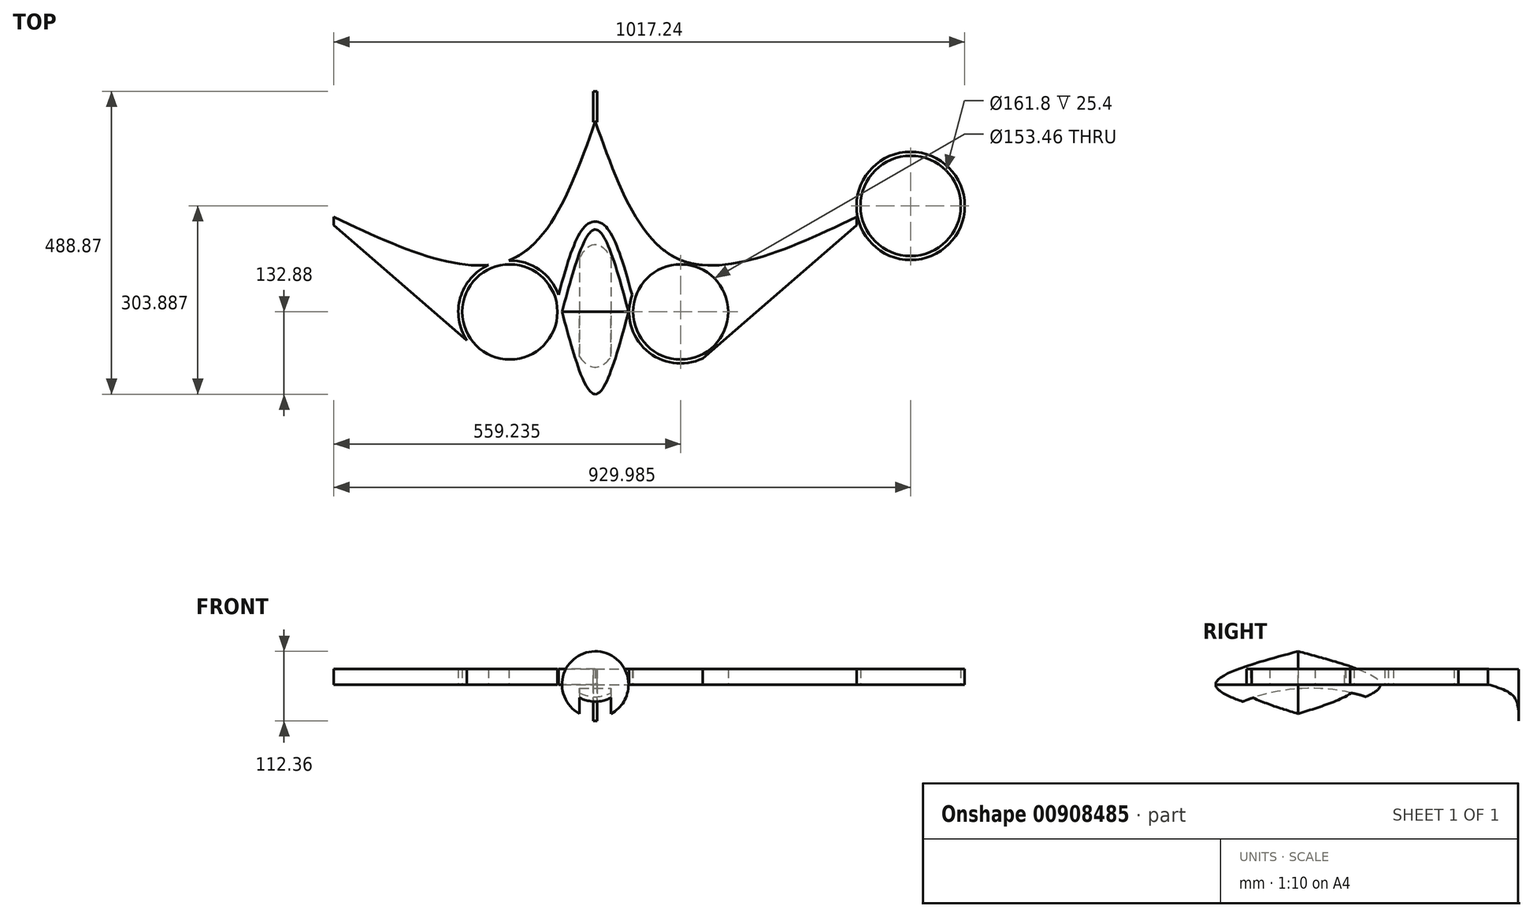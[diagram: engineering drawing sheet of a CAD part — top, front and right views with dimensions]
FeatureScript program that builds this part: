
annotation { "Feature Type Name" : "Feature", "Feature Type Description" : "" }
export const myFeature = defineFeature(function(context is Context, id is Id, definition is map)
    precondition{}
    {
        {
            var Q0;
            Q0=qCreatedBy(makeId("Top.planeOp"),FACE);
            var sketch = newSketch(context, id + "F0", { "sketchPlane" : qUnion([Q0])});
            skFitSpline(sketch, "E0", {"points": [v(-53.6, 0) * mm, v(0, -132.88) * mm, v(53.6, 0) * mm], "startDerivative": vector(107.2, -398.65) * mm, "endDerivative": vector(107.2, 398.65) * mm});
            skLineSegment(sketch, "E1", {"start": v(-53.6, 0) * mm, "end": v(53.6, 0) * mm});
            skFitSpline(sketch, "E2.MirrorCS", {"points": [v(-53.6, 0) * mm, v(0, 132.88) * mm, v(53.6, 0) * mm], "startDerivative": vector(107.2, 398.65) * mm, "endDerivative": vector(107.2, -398.65) * mm});
            skLineSegment(sketch, "E3", {"start": v(-46.29, -27.03) * mm, "end": v(-53.6, 0) * mm});
            skLineSegment(sketch, "E4", {"start": v(-46.29, 27.03) * mm, "end": v(-53.6, 0) * mm});
            skLineSegment(sketch, "E5", {"start": v(0, 132.88) * mm, "end": v(0, -132.88) * mm});
            skSolve(sketch);
        }
        {
            var Q0;
            Q0 = qSketchRegion(id + "F0", true);
            var sketch = newSketch(context, id + "F1", { "sketchPlane" : qUnion([Q0])});
            skCircle(sketch, "E6", {"center": v(137.74, 0) * mm, "radius": 76.73 * mm});
            skLineSegment(sketch, "E7", {"start": v(0, 0) * mm, "end": v(0, 75.52) * mm});
            skLineSegment(sketch, "E8", {"start": v(0, 75.52) * mm, "end": v(0, -130.45) * mm});
            skCircle(sketch, "E9.MirrorC", {"center": v(-137.74, 0) * mm, "radius": 76.73 * mm});
            skCircle(sketch, "E10.0", {"center": v(137.74, 0) * mm, "radius": 83.08 * mm});
            skCircle(sketch, "E11.MirrorC", {"center": v(-137.74, 0) * mm, "radius": 83.08 * mm});
            skFitSpline(sketch, "E12.0", {"points": [v(-65.86, 3.3) * mm, v(-63.63, 11.6) * mm, v(-59.16, 28.24) * mm, v(-52.41, 52.53) * mm, v(-46.76, 71.58) * mm, v(-42.2, 85.75) * mm, v(-38.76, 95.76) * mm, v(-35.28, 105.07) * mm, v(-31.74, 113.62) * mm, v(-28.1, 121.35) * mm, v(-24.91, 127.1) * mm, v(-22.2, 131.29) * mm, v(-20.04, 134.23) * mm, v(-17.7, 136.97) * mm, v(-15.1, 139.51) * mm, v(-12.14, 141.82) * mm, v(-9.24, 143.46) * mm, v(-6.63, 144.5) * mm, v(-4.53, 145.1) * mm, v(-2.68, 145.43) * mm, v(-1.15, 145.56) * mm, v(0, 145.6) * mm, v(1.16, 145.56) * mm, v(2.68, 145.43) * mm, v(4.53, 145.1) * mm, v(6.63, 144.5) * mm, v(9.24, 143.46) * mm, v(12.14, 141.82) * mm, v(15.1, 139.51) * mm, v(17.7, 136.97) * mm, v(20.04, 134.23) * mm, v(22.2, 131.29) * mm, v(24.91, 127.1) * mm, v(28.1, 121.35) * mm, v(31.74, 113.62) * mm, v(35.28, 105.07) * mm, v(38.76, 95.76) * mm, v(42.2, 85.75) * mm, v(46.76, 71.58) * mm, v(52.41, 52.53) * mm, v(59.16, 28.24) * mm, v(63.63, 11.6) * mm, v(65.86, 3.3) * mm]});
            skLineSegment(sketch, "E13", {"start": v(0, 75.52) * mm, "end": v(0, 307.36) * mm});
            skFitSpline(sketch, "E14", {"points": [v(0, 307.36) * mm, v(139.15, 83.07) * mm, v(457.3, 171) * mm], "startDerivative": vector(222.05, -626.73) * mm, "endDerivative": vector(683.94, 336.1) * mm});
            skFitSpline(sketch, "E15.MirrorCS", {"points": [v(0, 307.36) * mm, v(-139.15, 83.07) * mm, v(-457.3, 171) * mm], "startDerivative": vector(-222.05, -626.73) * mm, "endDerivative": vector(-683.94, 336.1) * mm});
            skLineSegment(sketch, "E16", {"start": v(173.26, -75.1) * mm, "end": v(421.49, 139.98) * mm});
            skLineSegment(sketch, "E17.MirrorCS", {"start": v(-173.26, -75.1) * mm, "end": v(-421.49, 139.98) * mm});
            skLineSegment(sketch, "E18", {"start": v(421.49, 139.98) * mm, "end": v(421.49, 153.48) * mm});
            skLineSegment(sketch, "E19.MirrorCS", {"start": v(-421.49, 139.98) * mm, "end": v(-421.49, 153.48) * mm});
            skCircle(sketch, "E20", {"center": v(508.5, 171) * mm, "radius": 87.25 * mm});
            skCircle(sketch, "E21.MirrorC", {"center": v(-508.5, 171) * mm, "radius": 87.25 * mm});
            skCircle(sketch, "E22.0", {"center": v(508.5, 171) * mm, "radius": 80.9 * mm});
            skCircle(sketch, "E23.MirrorC", {"center": v(-508.5, 171) * mm, "radius": 80.9 * mm});
            skLineSegment(sketch, "E24.extension", {"start": v(-58.53, 30.38) * mm, "end": v(-59.34, 27.46) * mm});
            skSolve(sketch);
        }
        {
            var Q0;
            {var subQ5=sQuery(id+"F1.wireOp",EDGE,"E18");Q0=makeQuery(id+"F1.imprint","IMPRINT",FACE,{"disambiguationData":[TD([[makeQuery(id+"F1.imprint","IMPRINT",EDGE,{"derivedFrom":subQ5}),1.0]])]});}
            var Q1;
            {var subQ0=sQuery(id+"F1.wireOp",EDGE,"E12.0");var subQ1=sQuery(id+"F1.wireOp",EDGE,"E10.0");var subQ2=makeQuery(id+"F1.imprint","INTERSECT",VERTEX,{"derivedFrom":[subQ1,subQ0]});Q1=makeQuery(id+"F1.imprint","IMPRINT",FACE,{"disambiguationData":[TD([[makeQuery(id+"F1.imprint","IMPRINT",EDGE,{"disambiguationData":[TD([[subQ2,1.0]])],"derivedFrom":subQ1}),-1.0]])]});}
            var Q2;
            {var subQ0=sQuery(id+"F1.wireOp",EDGE,"E24.extension");var subQ7=sQuery(id+"F1.wireOp",EDGE,"E12.0");var subQ9=makeQuery(id+"F1.imprint","INTERSECT",VERTEX,{"derivedFrom":[subQ7,subQ0]});Q2=makeQuery(id+"F1.imprint","IMPRINT",FACE,{"disambiguationData":[TD([[makeQuery(id+"F1.imprint","IMPRINT",EDGE,{"disambiguationData":[TD([[subQ9,-1.0]])],"derivedFrom":subQ7}),1.0]])]});}
            var Q3;
            {var subQ0=sQuery(id+"F1.wireOp",EDGE,"E19.MirrorCS");Q3=makeQuery(id+"F1.imprint","IMPRINT",FACE,{"disambiguationData":[TD([[makeQuery(id+"F1.imprint","IMPRINT",EDGE,{"derivedFrom":subQ0}),-1.0]])]});}
            var Q4;
            Q4=makeQuery(id+"F1.imprint","IMPRINT",FACE,{"disambiguationData":[TD([[makeQuery(id+"F1.imprint","IMPRINT",EDGE,{"derivedFrom":sQuery(id+"F1.wireOp",EDGE,"E9.MirrorC")}),1.0]])]});
            var Q5;
            Q5=makeQuery(id+"F1.imprint","IMPRINT",FACE,{"disambiguationData":[TD([[makeQuery(id+"F1.imprint","IMPRINT",EDGE,{"derivedFrom":sQuery(id+"F1.wireOp",EDGE,"E6")}),-1.0]])]});
            var Q6;
            Q6=makeQuery(id+"F1.imprint","IMPRINT",FACE,{"disambiguationData":[TD([[makeQuery(id+"F1.imprint","IMPRINT",EDGE,{"derivedFrom":sQuery(id+"F1.wireOp",EDGE,"E20")}),1.0]])]});
            var Q7;
            Q7=makeQuery(id+"F1.imprint","IMPRINT",FACE,{"disambiguationData":[TD([[makeQuery(id+"F1.imprint","IMPRINT",EDGE,{"derivedFrom":sQuery(id+"F1.wireOp",EDGE,"E21.MirrorC")}),-1.0]])]});
            extrude(context, id + "F2", {"entities" : qUnion([Q0, Q1, Q2, Q3, Q4, Q5, Q6, Q7]), "depth" : 25.4 * mm, "offsetDistance" : 25.4 * mm});
        }
        {
            var Q0;
            {var subQ0=sQuery(id+"F0.wireOp",EDGE,"E2.MirrorCS");var subQ3=sQuery(id+"F0.wireOp",EDGE,"E5");var subQ5=makeQuery(id+"F0.imprint","INTERSECT",VERTEX,{"derivedFrom":[subQ0,subQ3]});Q0=makeQuery(id+"F0.imprint","IMPRINT",FACE,{"disambiguationData":[TD([[makeQuery(id+"F0.imprint","IMPRINT",EDGE,{"disambiguationData":[TD([[subQ5,-1.0]])],"derivedFrom":subQ3}),1.0]])]});}
            var Q1;
            {var subQ1=sQuery(id+"F0.wireOp",EDGE,"E0");var subQ3=sQuery(id+"F0.wireOp",EDGE,"E5");var subQ4=makeQuery(id+"F0.imprint","INTERSECT",VERTEX,{"derivedFrom":[subQ1,subQ3]});Q1=makeQuery(id+"F0.imprint","IMPRINT",FACE,{"disambiguationData":[TD([[makeQuery(id+"F0.imprint","IMPRINT",EDGE,{"disambiguationData":[TD([[subQ4,1.0]])],"derivedFrom":subQ3}),1.0]])]});}
            var Q2;
            Q2=sQuery(id+"F0.wireOp",EDGE,"E5");
            revolve(context, id + "F3", {"surfaceOperationType" : NewSurfaceOperationType.NEW, "entities" : qUnion([Q0, Q1]), "axis" : qUnion([Q2]), "revolveType" : RevolveType.FULL});
        }
        {
            var Q0;
            Q0=qCreatedBy(makeId("Right.planeOp"),FACE);
            var sketch = newSketch(context, id + "F4", { "sketchPlane" : qUnion([Q0])});
            skArc(sketch, "E25", {"start": v(116.82, -22.27) * mm, "mid": v(12.81, -6.12) * mm, "end": v(-90.17, -27.87) * mm});
            skLineSegment(sketch, "E26", {"start": v(116.82, -22.27) * mm, "end": v(0, -56.15) * mm});
            skLineSegment(sketch, "E27", {"start": v(0, -56.15) * mm, "end": v(-90.17, -27.87) * mm});
            skSolve(sketch);
        }
        {
            var Q0;
            Q0 = qSketchRegion(id + "F4", true);
            extrude(context, id + "F5", {"entities" : qUnion([Q0]), "operationType" : NewBodyOperationType.REMOVE, "oppositeDirection" : true, "depth" : 25.4 * mm, "offsetDistance" : 25.4 * mm, "hasSecondDirection" : true, "secondDirectionOppositeDirection" : false, "secondDirectionDepth" : 25.4 * mm});
        }
        {
            var Q0;
            Q0=qCreatedBy(makeId("Right.planeOp"),FACE);
            var sketch = newSketch(context, id + "F6", { "sketchPlane" : qUnion([Q0])});
            skFitSpline(sketch, "E28", {"points": [v(306.28, 0) * mm, v(348.43, -20.22) * mm, v(355.99, -58.76) * mm], "startDerivative": vector(97.73, -27.83) * mm, "endDerivative": vector(0.26, -90.6) * mm});
            skLineSegment(sketch, "E29", {"start": v(355.99, -58.76) * mm, "end": v(355.94, 0) * mm});
            skLineSegment(sketch, "E30", {"start": v(355.94, 0) * mm, "end": v(306.28, 0) * mm});
            skLineSegment(sketch, "E31", {"start": v(355.94, 0) * mm, "end": v(355.94, 24.64) * mm});
            skLineSegment(sketch, "E32", {"start": v(355.94, 24.64) * mm, "end": v(306.28, 25) * mm});
            skLineSegment(sketch, "E33", {"start": v(306.28, 25) * mm, "end": v(306.28, 0) * mm});
            skSolve(sketch);
        }
        {
            var Q0;
            Q0 = qSketchRegion(id + "F6", true);
            extrude(context, id + "F7", {"entities" : qUnion([Q0]), "operationType" : NewBodyOperationType.ADD, "oppositeDirection" : true, "depth" : 3.17 * mm, "offsetDistance" : 25.4 * mm, "hasSecondDirection" : true, "secondDirectionOppositeDirection" : false, "secondDirectionDepth" : 3.17 * mm});
        }
    });
